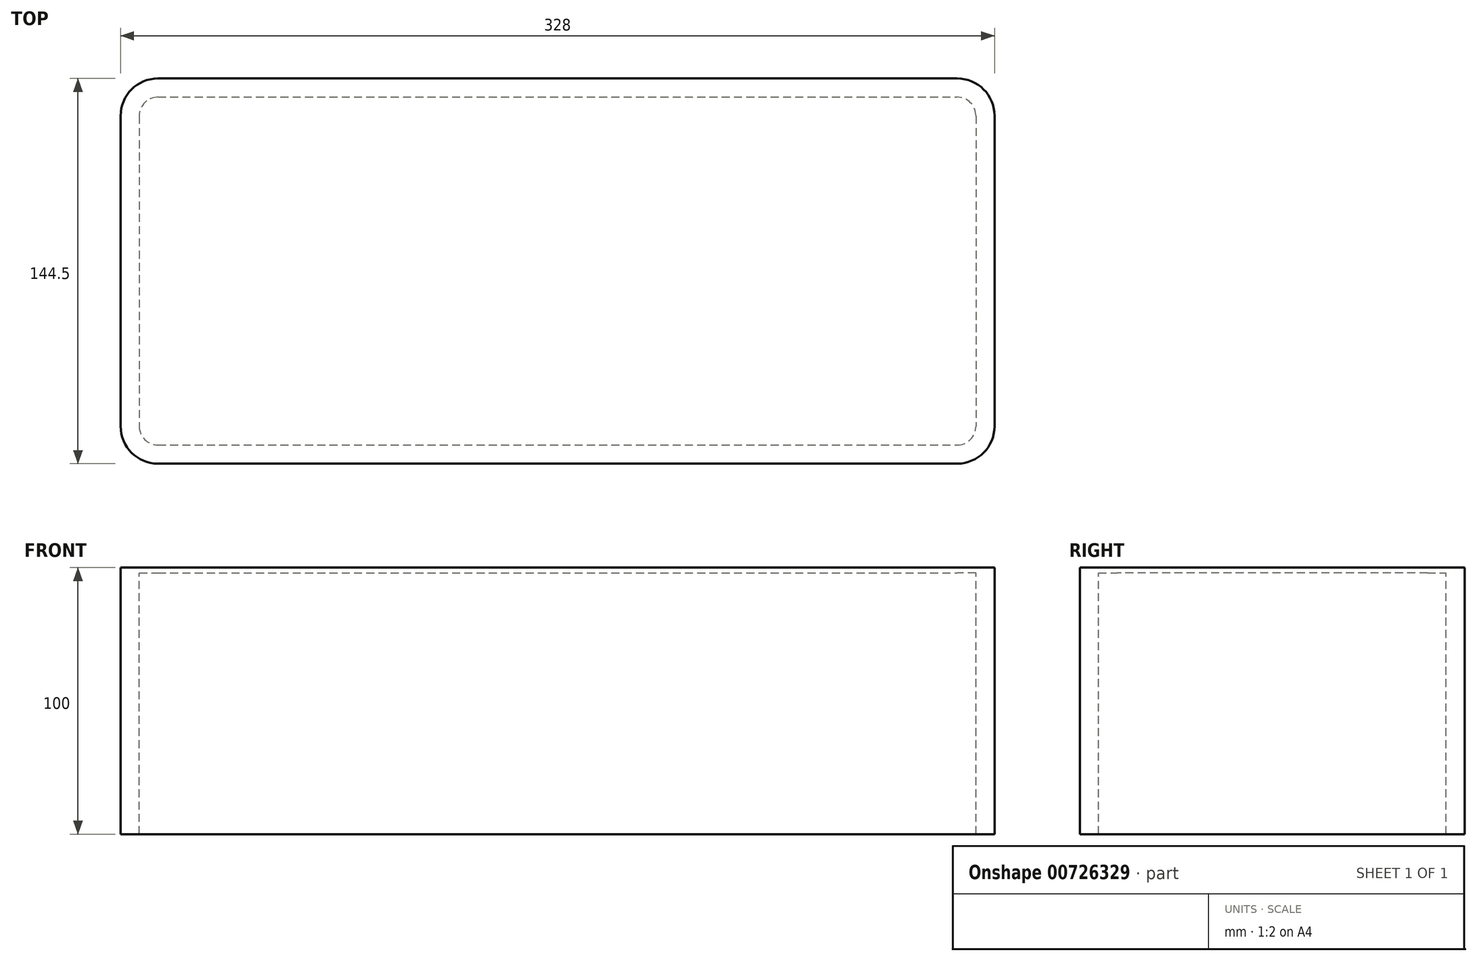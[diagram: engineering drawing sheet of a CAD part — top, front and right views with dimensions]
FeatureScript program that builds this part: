
annotation { "Feature Type Name" : "Feature", "Feature Type Description" : "" }
export const myFeature = defineFeature(function(context is Context, id is Id, definition is map)
    precondition{}
    {
        {
            var Q0;
            Q0=qCreatedBy(makeId("Top.planeOp"),FACE);
            var sketch = newSketch(context, id + "F0", { "sketchPlane" : qUnion([Q0])});
            skLineSegment(sketch, "E0.bottom", {"start": v(-149.79, 65.16) * mm, "end": v(150.21, 65.16) * mm});
            skLineSegment(sketch, "E0.top", {"start": v(-149.79, -65.34) * mm, "end": v(150.21, -65.34) * mm});
            skLineSegment(sketch, "E0.left", {"start": v(-156.79, 58.16) * mm, "end": v(-156.79, -58.34) * mm});
            skLineSegment(sketch, "E0.right", {"start": v(157.21, 58.16) * mm, "end": v(157.21, -58.34) * mm});
            skPoint(sketch, "E1.visualSharp", {"position": v(-156.79, 65.16) * mm});
            skArc(sketch, "E1.filletArc", {"start": v(-149.79, 65.16) * mm, "mid": v(-154.74, 63.11) * mm, "end": v(-156.79, 58.16) * mm});
            skPoint(sketch, "E2.visualSharp", {"position": v(157.21, 65.16) * mm});
            skArc(sketch, "E2.filletArc", {"start": v(157.21, 58.16) * mm, "mid": v(155.16, 63.11) * mm, "end": v(150.21, 65.16) * mm});
            skPoint(sketch, "E3.visualSharp", {"position": v(157.21, -65.34) * mm});
            skArc(sketch, "E3.filletArc", {"start": v(150.21, -65.34) * mm, "mid": v(155.16, -63.3) * mm, "end": v(157.21, -58.34) * mm});
            skPoint(sketch, "E4.visualSharp", {"position": v(-156.79, -65.34) * mm});
            skArc(sketch, "E4.filletArc", {"start": v(-156.79, -58.34) * mm, "mid": v(-154.74, -63.3) * mm, "end": v(-149.79, -65.34) * mm});
            skArc(sketch, "E5.0", {"start": v(-149.79, 72.16) * mm, "mid": v(-159.69, 68.06) * mm, "end": v(-163.79, 58.16) * mm});
            skLineSegment(sketch, "E5.1", {"start": v(-149.79, 72.16) * mm, "end": v(150.21, 72.16) * mm});
            skLineSegment(sketch, "E5.2", {"start": v(-163.79, 58.16) * mm, "end": v(-163.79, -58.34) * mm});
            skArc(sketch, "E5.3", {"start": v(164.21, 58.16) * mm, "mid": v(160.11, 68.06) * mm, "end": v(150.21, 72.16) * mm});
            skArc(sketch, "E5.4", {"start": v(-163.79, -58.34) * mm, "mid": v(-159.69, -68.24) * mm, "end": v(-149.79, -72.34) * mm});
            skLineSegment(sketch, "E5.5", {"start": v(-149.79, -72.34) * mm, "end": v(150.21, -72.34) * mm});
            skArc(sketch, "E5.6", {"start": v(150.21, -72.34) * mm, "mid": v(160.11, -68.24) * mm, "end": v(164.21, -58.34) * mm});
            skLineSegment(sketch, "E5.7", {"start": v(164.21, 58.16) * mm, "end": v(164.21, -58.34) * mm});
            skSolve(sketch);
        }
        {
            var Q0;
            Q0 = qSketchRegion(id + "F0", true);
            extrude(context, id + "F1", {"entities" : qUnion([Q0]), "depth" : -100 * mm, "offsetDistance" : 25 * mm});
        }
        {
            var Q0;
            Q0=makeQuery(id+"F0.imprint","IMPRINT",FACE,{"disambiguationData":[TD([[makeQuery(id+"F0.imprint","IMPRINT",EDGE,{"derivedFrom":sQuery(id+"F0.wireOp",EDGE,"E0.bottom")}),-1.0]])]});
            extrude(context, id + "F2", {"entities" : qUnion([Q0]), "operationType" : NewBodyOperationType.ADD, "depth" : -2 * mm, "offsetDistance" : 25 * mm});
        }
    });
